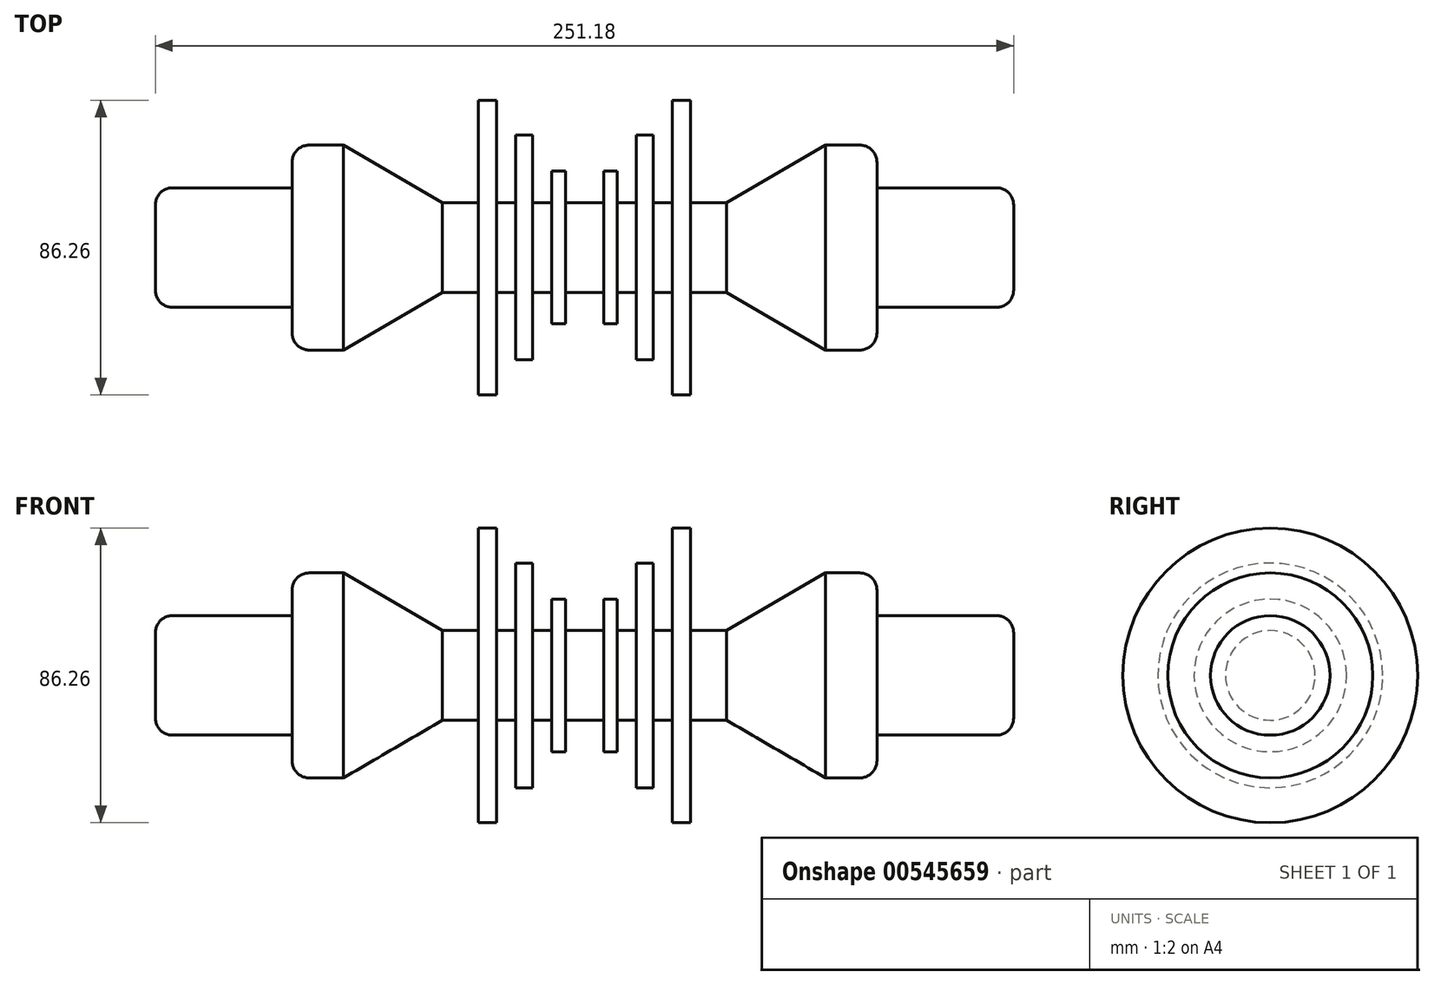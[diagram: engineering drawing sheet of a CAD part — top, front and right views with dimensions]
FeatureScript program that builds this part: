
annotation { "Feature Type Name" : "Feature", "Feature Type Description" : "" }
export const myFeature = defineFeature(function(context is Context, id is Id, definition is map)
    precondition{}
    {
        {
            var Q0;
            Q0=qCreatedBy(makeId("Front.planeOp"),FACE);
            var sketch = newSketch(context, id + "F0", { "sketchPlane" : qUnion([Q0])});
            skLineSegment(sketch, "E0", {"start": v(0, 0) * mm, "end": v(0, 13.12) * mm});
            skLineSegment(sketch, "E1", {"start": v(70.55, 30) * mm, "end": v(85.59, 30) * mm});
            skLineSegment(sketch, "E2", {"start": v(85.59, 30) * mm, "end": v(85.59, 17.5) * mm});
            skLineSegment(sketch, "E3", {"start": v(85.59, 17.5) * mm, "end": v(125.59, 17.5) * mm});
            skLineSegment(sketch, "E4", {"start": v(125.59, 17.5) * mm, "end": v(125.59, 0) * mm});
            skLineSegment(sketch, "E5", {"start": v(125.59, 0) * mm, "end": v(0, 0) * mm});
            skLineSegment(sketch, "E6", {"start": v(0, 13.12) * mm, "end": v(5.59, 13.12) * mm});
            skLineSegment(sketch, "E7", {"start": v(5.59, 13.12) * mm, "end": v(5.59, 22.34) * mm});
            skLineSegment(sketch, "E8", {"start": v(5.59, 22.34) * mm, "end": v(9.62, 22.34) * mm});
            skLineSegment(sketch, "E9", {"start": v(9.62, 22.34) * mm, "end": v(9.62, 13.12) * mm});
            skLineSegment(sketch, "E10", {"start": v(9.62, 13.12) * mm, "end": v(15.2, 13.12) * mm});
            skLineSegment(sketch, "E11", {"start": v(15.2, 13.12) * mm, "end": v(15.2, 32.89) * mm});
            skLineSegment(sketch, "E12", {"start": v(15.2, 32.89) * mm, "end": v(20.17, 32.89) * mm});
            skLineSegment(sketch, "E13", {"start": v(20.17, 32.89) * mm, "end": v(20.17, 13.12) * mm});
            skLineSegment(sketch, "E14", {"start": v(20.17, 13.12) * mm, "end": v(25.75, 13.12) * mm});
            skLineSegment(sketch, "E15", {"start": v(25.75, 13.12) * mm, "end": v(25.75, 43.13) * mm});
            skLineSegment(sketch, "E16", {"start": v(25.75, 43.13) * mm, "end": v(31.03, 43.13) * mm});
            skLineSegment(sketch, "E17", {"start": v(31.03, 43.13) * mm, "end": v(31.03, 13.12) * mm});
            skLineSegment(sketch, "E18", {"start": v(31.03, 13.12) * mm, "end": v(41.58, 13.12) * mm});
            skLineSegment(sketch, "E19", {"start": v(41.58, 13.12) * mm, "end": v(70.55, 30) * mm});
            skSolve(sketch);
        }
        {
            var Q0;
            Q0=makeQuery(id+"F0.imprint","IMPRINT",FACE,{"disambiguationData":[TD([[makeQuery(id+"F0.imprint","IMPRINT",EDGE,{"derivedFrom":sQuery(id+"F0.wireOp",EDGE,"E0")}),-1.0]])]});
            var Q1;
            Q1=sQuery(id+"F0.wireOp",EDGE,"E5");
            revolve(context, id + "F1", {"entities" : qUnion([Q0]), "axis" : qUnion([Q1]), "revolveType" : RevolveType.FULL});
        }
        {
            var Q0;
            Q0=makeQuery(id+"F1.opRevolve","SWEPT_BODY",BODY,{"disambiguationData":[OSD([sQuery(id+"F0.wireOp",EDGE,"E0"),sQuery(id+"F0.wireOp",EDGE,"a8409ff0-ee09-4b80-9a28-8479c8c301c4"),sQuery(id+"F0.wireOp",EDGE,"E1"),sQuery(id+"F0.wireOp",EDGE,"E2"),sQuery(id+"F0.wireOp",EDGE,"E3"),sQuery(id+"F0.wireOp",EDGE,"E4"),sQuery(id+"F0.wireOp",EDGE,"E5")])]});
            var Q1;
            Q1=makeQuery(id+"F1.opRevolve","SWEPT_FACE",FACE,{"disambiguationData":[OSD([sQuery(id+"F0.wireOp",EDGE,"E0")])]});
            mirror(context, id + "F2", {"operationType" : NewBodyOperationType.ADD, "entities" : qUnion([Q0]), "mirrorPlane" : qUnion([Q1])});
        }
        {
            var Q0;
            Q0=makeQuery(id+"F2.opPattern","COPY",EDGE,{"derivedFrom":makeQuery(id+"F1.opRevolve","SWEPT_EDGE",EDGE,{"disambiguationData":[OSD([sQuery(id+"F0.wireOp",EDGE,"E1"),sQuery(id+"F0.wireOp",EDGE,"E2")])]}),"instanceName":"1"});
            var Q1;
            Q1=makeQuery(id+"F1.opRevolve","SWEPT_EDGE",EDGE,{"disambiguationData":[OSD([sQuery(id+"F0.wireOp",EDGE,"E1"),sQuery(id+"F0.wireOp",EDGE,"E2")])]});
            var Q2;
            Q2=makeQuery(id+"F1.opRevolve","SWEPT_EDGE",EDGE,{"disambiguationData":[OSD([sQuery(id+"F0.wireOp",EDGE,"E3"),sQuery(id+"F0.wireOp",EDGE,"E4")])]});
            var Q3;
            Q3=makeQuery(id+"F2.opPattern","COPY",EDGE,{"derivedFrom":makeQuery(id+"F1.opRevolve","SWEPT_EDGE",EDGE,{"disambiguationData":[OSD([sQuery(id+"F0.wireOp",EDGE,"E3"),sQuery(id+"F0.wireOp",EDGE,"E4")])]}),"instanceName":"1"});
            fillet(context, id + "F3", {"entities" : qUnion([Q0, Q1, Q2, Q3]), "radius" : 5 * mm, "tangentPropagation" : true, "allowEdgeOverflow" : false});
        }
    });
